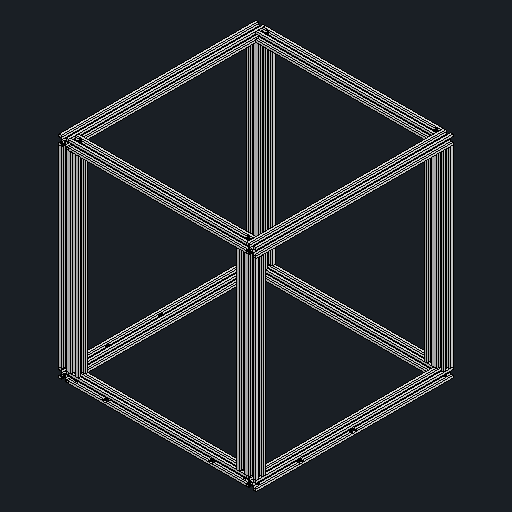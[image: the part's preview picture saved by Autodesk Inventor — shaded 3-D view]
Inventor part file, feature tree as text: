
AUTODESK INVENTOR PART (.ipt)
format: ipt  version: 2024.2 (Build 282272000, 272)  size: 1,010,688 bytes
history: native  units: mm
features: other x16, mirror x8
ambient origin geometry x8: Origin, YZ Plane, XZ Plane, XY Plane, X Axis, Y Axis, Z Axis, Center Point
bodies: Body1 (feature_tree), Body2 (feature_tree), Body3 (feature_tree), Body4 (feature_tree), Body5 (feature_tree), Body6 (feature_tree), Body7 (feature_tree), Body8 (feature_tree), Body9 (feature_tree), Body10 (feature_tree), Body11 (feature_tree), Body12 (feature_tree)
feature tree (24):
  other  "솔리드1"
  other  "솔리드2"
  other  "솔리드3"
  other  "솔리드4"
  other  "솔리드5"
  other  "솔리드6"
  other  "솔리드7"
  other  "솔리드8"
  other  "솔리드9"
  other  "솔리드10"
  other  "솔리드11"
  other  "솔리드12"
  other  "CBORE for M5 Hex Head Bolt2-mainborad[1]"
  other  "M5x0.8 Tapped Hole4-corner-pulleys[1]"
  other  "M5x0.8 Tapped Hole4-corner-pulleys[2]"
  mirror  "Mirror26-corner-pulleys[1]"
  other  "M5x0.8 Tapped Hole5-corner-brackets[1]"
  mirror  "Mirror27-corner-brackets[1]"
  mirror  "Mirror27-corner-brackets[2]"
  mirror  "Mirror28-corner-brackets[1]"
  mirror  "Mirror30-corner-brackets[1]"
  mirror  "Mirror30-corner-brackets[2]"
  mirror  "Mirror30-corner-brackets[3]"
  mirror  "Mirror26-corner-pulleys[3]"
